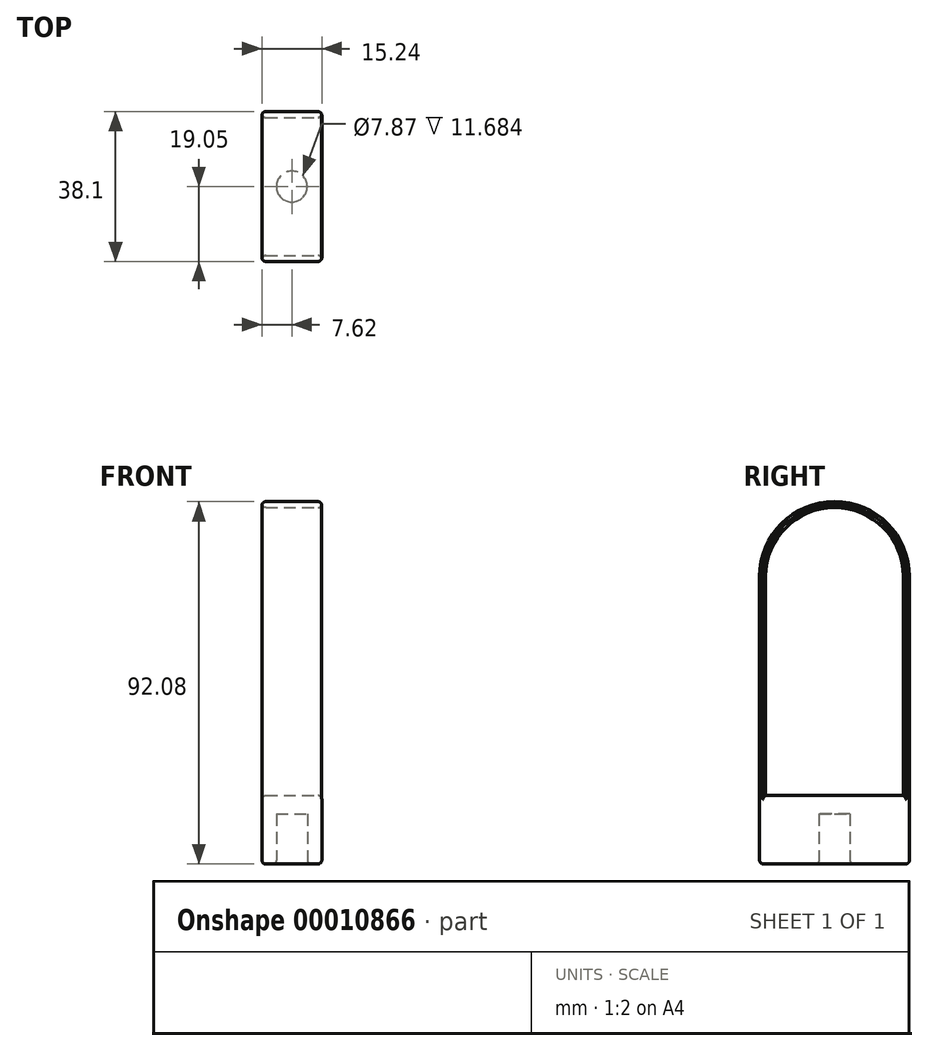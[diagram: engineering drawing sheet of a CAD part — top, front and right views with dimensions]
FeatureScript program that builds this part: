
annotation { "Feature Type Name" : "Feature", "Feature Type Description" : "" }
export const myFeature = defineFeature(function(context is Context, id is Id, definition is map)
    precondition{}
    {
        {
            var Q0;
            Q0=qCreatedBy(makeId("Top.planeOp"),FACE);
            var sketch = newSketch(context, id + "F0", { "sketchPlane" : qUnion([Q0])});
            skLineSegment(sketch, "E0.bottom", {"start": v(0, 0) * mm, "end": v(15.24, 0) * mm});
            skLineSegment(sketch, "E0.top", {"start": v(0, 38.1) * mm, "end": v(15.24, 38.1) * mm});
            skLineSegment(sketch, "E0.left", {"start": v(0, 0) * mm, "end": v(0, 38.1) * mm});
            skLineSegment(sketch, "E0.right", {"start": v(15.24, 0) * mm, "end": v(15.24, 38.1) * mm});
            skSolve(sketch);
        }
        {
            var Q0;
            Q0=makeQuery(id+"F0.imprint","IMPRINT",FACE,{"disambiguationData":[TD([[makeQuery(id+"F0.imprint","IMPRINT",EDGE,{"derivedFrom":sQuery(id+"F0.wireOp",EDGE,"E0.bottom")}),1.0]])]});
            extrude(context, id + "F1", {"entities" : qUnion([Q0]), "depth" : 76.2 * mm});
        }
        {
            var Q0;
            Q0=makeQuery(id+"F1.opExtrude","SWEPT_FACE",FACE,{"disambiguationData":[OSD([sQuery(id+"F0.wireOp",EDGE,"E0.right")])]});
            var sketch = newSketch(context, id + "F2", { "sketchPlane" : qUnion([Q0])});
            skArc(sketch, "E1", {"start": v(38.1, 57.15) * mm, "mid": v(19.05, 76.2) * mm, "end": v(0, 57.15) * mm});
            skPoint(sketch, "E1.centerSnap0", {"position": v(19.05, 76.2) * mm});
            skLineSegment(sketch, "E2", {"start": v(38.1, 15.88) * mm, "end": v(0, 15.87) * mm});
            skSolve(sketch);
        }
        {
            var Q0;
            {var subQ0=sQuery(id+"F2.wireOp",EDGE,"E1");var subQ1=sQuery(id+"F0.wireOp",EDGE,"E0.right");var subQ4=makeQuery(id+"F1.opExtrude","CAP_EDGE",EDGE,{"disambiguationData":[OSD([subQ1])],"isStart":false});var subQ5=makeQuery(id+"F2.imprint","INTERSECT",VERTEX,{"derivedFrom":[subQ4,subQ0]});Q0=makeQuery(id+"F2.imprint","IMPRINT",FACE,{"disambiguationData":[TD([[makeQuery(id+"F2.imprint","IMPRINT",EDGE,{"disambiguationData":[TD([[subQ5,1.0]])],"derivedFrom":subQ0}),-1.0]])]});}
            var Q1;
            {var subQ0=sQuery(id+"F2.wireOp",EDGE,"E1");var subQ1=sQuery(id+"F0.wireOp",EDGE,"E0.right");var subQ4=makeQuery(id+"F1.opExtrude","CAP_EDGE",EDGE,{"disambiguationData":[OSD([subQ1])],"isStart":false});var subQ5=makeQuery(id+"F2.imprint","INTERSECT",VERTEX,{"derivedFrom":[subQ4,subQ0]});Q1=makeQuery(id+"F2.imprint","IMPRINT",FACE,{"disambiguationData":[TD([[makeQuery(id+"F2.imprint","IMPRINT",EDGE,{"disambiguationData":[TD([[subQ5,-1.0]])],"derivedFrom":subQ0}),-1.0]])]});}
            extrude(context, id + "F3", {"entities" : qUnion([Q0, Q1]), "operationType" : NewBodyOperationType.REMOVE, "oppositeDirection" : true, "depth" : 25.4 * mm});
        }
        {
            var Q0;
            Q0=makeQuery(id+"F1.opExtrude","SWEPT_FACE",FACE,{"disambiguationData":[OSD([sQuery(id+"F0.wireOp",EDGE,"E0.right")])]});
            var Q1;
            Q1=makeQuery(id+"F1.opExtrude","SWEPT_FACE",FACE,{"disambiguationData":[OSD([sQuery(id+"F0.wireOp",EDGE,"E0.left")])]});
            shell(context, id + "F4", {"entities" : qUnion([Q0, Q1]), "thickness" : 1.52 * mm});
        }
        {
            var Q0;
            Q0=makeQuery(id+"F1.opExtrude","CAP_FACE",FACE,{"disambiguationData":[OSD([sQuery(id+"F0.wireOp",EDGE,"E0.bottom"),sQuery(id+"F0.wireOp",EDGE,"E0.top"),sQuery(id+"F0.wireOp",EDGE,"E0.left"),sQuery(id+"F0.wireOp",EDGE,"E0.right")])],"isStart":true});
            extrude(context, id + "F5", {"entities" : qUnion([Q0]), "operationType" : NewBodyOperationType.ADD, "depth" : 15.88 * mm});
        }
        {
            var Q0;
            Q0=makeQuery(id+"F5.opExtrude","CAP_FACE",FACE,{"disambiguationData":[OSD([sQuery(id+"F0.wireOp",EDGE,"E0.bottom"),sQuery(id+"F0.wireOp",EDGE,"E0.top"),sQuery(id+"F0.wireOp",EDGE,"E0.left"),sQuery(id+"F0.wireOp",EDGE,"E0.right")])],"isStart":false});
            var sketch = newSketch(context, id + "F6", { "sketchPlane" : qUnion([Q0])});
            skCircle(sketch, "E3", {"center": v(7.62, -19.05) * mm, "radius": 3.94 * mm});
            skPoint(sketch, "E3.centerSnap0", {"position": v(7.62, 0) * mm});
            skPoint(sketch, "E3.centerSnap1", {"position": v(15.24, -19.05) * mm});
            skSolve(sketch);
        }
        {
            var Q0;
            Q0=makeQuery(id+"F6.imprint","IMPRINT",FACE,{"disambiguationData":[TD([[makeQuery(id+"F6.imprint","IMPRINT",EDGE,{"derivedFrom":sQuery(id+"F6.wireOp",EDGE,"E3")}),1.0]])]});
            extrude(context, id + "F7", {"entities" : qUnion([Q0]), "operationType" : NewBodyOperationType.REMOVE, "oppositeDirection" : true, "depth" : 12.7 * mm});
        }
        {
            var Q0;
            Q0=makeQuery(id+"F5.opExtrude","CAP_FACE",FACE,{"disambiguationData":[OSD([sQuery(id+"F0.wireOp",EDGE,"E0.bottom"),sQuery(id+"F0.wireOp",EDGE,"E0.top"),sQuery(id+"F0.wireOp",EDGE,"E0.left"),sQuery(id+"F0.wireOp",EDGE,"E0.right")])],"isStart":false});
            var Q1;
            {var subQ0=sQuery(id+"F0.wireOp",EDGE,"E0.left");Q1=makeQuery(id+"F5.boolean.opBoolean","MERGE",FACE,{"derivedFrom":[makeQuery(id+"F1.opExtrude","SWEPT_FACE",FACE,{"disambiguationData":[OSD([subQ0])]}),makeQuery(id+"F5.opExtrude","SWEPT_FACE",FACE,{"disambiguationData":[OSD([subQ0])]})]});}
            var Q2;
            {var subQ0=sQuery(id+"F0.wireOp",EDGE,"E0.right");Q2=makeQuery(id+"F5.boolean.opBoolean","MERGE",FACE,{"derivedFrom":[makeQuery(id+"F1.opExtrude","SWEPT_FACE",FACE,{"disambiguationData":[OSD([subQ0])]}),makeQuery(id+"F5.opExtrude","SWEPT_FACE",FACE,{"disambiguationData":[OSD([subQ0])]})]});}
            fillet(context, id + "F8", {"entities" : qUnion([Q0, Q1, Q2]), "radius" : 1.02 * mm, "tangentPropagation" : true, "allowEdgeOverflow" : false});
        }
    });
